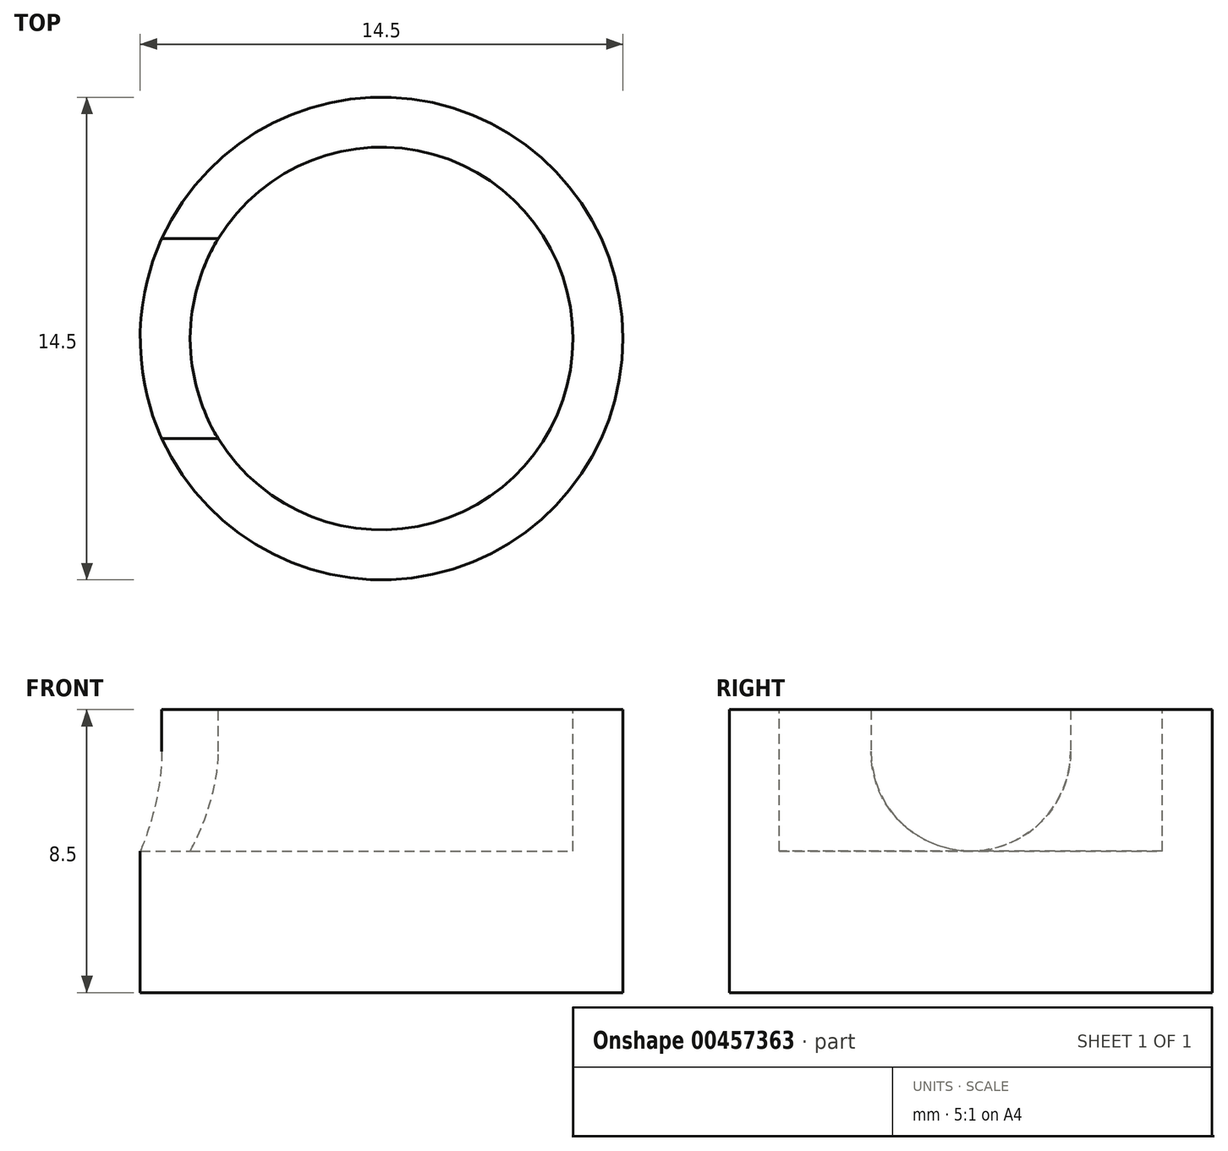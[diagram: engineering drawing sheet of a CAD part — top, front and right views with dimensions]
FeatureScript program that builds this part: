
annotation { "Feature Type Name" : "Feature", "Feature Type Description" : "" }
export const myFeature = defineFeature(function(context is Context, id is Id, definition is map)
    precondition{}
    {
        {
            var Q0;
            Q0=qCreatedBy(makeId("Top.planeOp"),FACE);
            var sketch = newSketch(context, id + "F0", { "sketchPlane" : qUnion([Q0])});
            skCircle(sketch, "E0", {"center": v(0, 0) * mm, "radius": 7.25 * mm});
            skSolve(sketch);
        }
        {
            var Q0;
            Q0 = qSketchRegion(id + "F0", true);
            extrude(context, id + "F1", {"entities" : qUnion([Q0]), "depth" : 8.5 * mm});
        }
        {
            var Q0;
            Q0=makeQuery(id+"F1.opExtrude","CAP_FACE",FACE,{"disambiguationData":[OSD([sQuery(id+"F0.wireOp",EDGE,"E0")])],"isStart":false});
            var sketch = newSketch(context, id + "F2", { "sketchPlane" : qUnion([Q0])});
            skCircle(sketch, "E1", {"center": v(0, 0) * mm, "radius": 5.75 * mm});
            skSolve(sketch);
        }
        {
            var Q0;
            Q0 = qSketchRegion(id + "F2", true);
            extrude(context, id + "F3", {"entities" : qUnion([Q0]), "operationType" : NewBodyOperationType.REMOVE, "oppositeDirection" : true, "depth" : 4.25 * mm});
        }
        {
            var Q0;
            Q0=qCreatedBy(makeId("Right.planeOp"),FACE);
            var sketch = newSketch(context, id + "F4", { "sketchPlane" : qUnion([Q0])});
            skLineSegment(sketch, "E2", {"start": v(5.75, 4.25) * mm, "end": v(-5.75, 4.25) * mm, "construction": true});
            skArc(sketch, "E3", {"start": v(-3, 7.25) * mm, "mid": v(0, 4.25) * mm, "end": v(3, 7.25) * mm});
            skLineSegment(sketch, "E4", {"start": v(-3, 7.25) * mm, "end": v(-3, 9) * mm});
            skLineSegment(sketch, "E5", {"start": v(3, 7.25) * mm, "end": v(3, 9.04) * mm});
            skLineSegment(sketch, "E6", {"start": v(3, 9.04) * mm, "end": v(-3, 9) * mm});
            skSolve(sketch);
        }
        {
            var Q0;
            Q0 = qSketchRegion(id + "F4", true);
            extrude(context, id + "F5", {"entities" : qUnion([Q0]), "operationType" : NewBodyOperationType.REMOVE, "oppositeDirection" : true, "depth" : 25 * mm});
        }
    });
